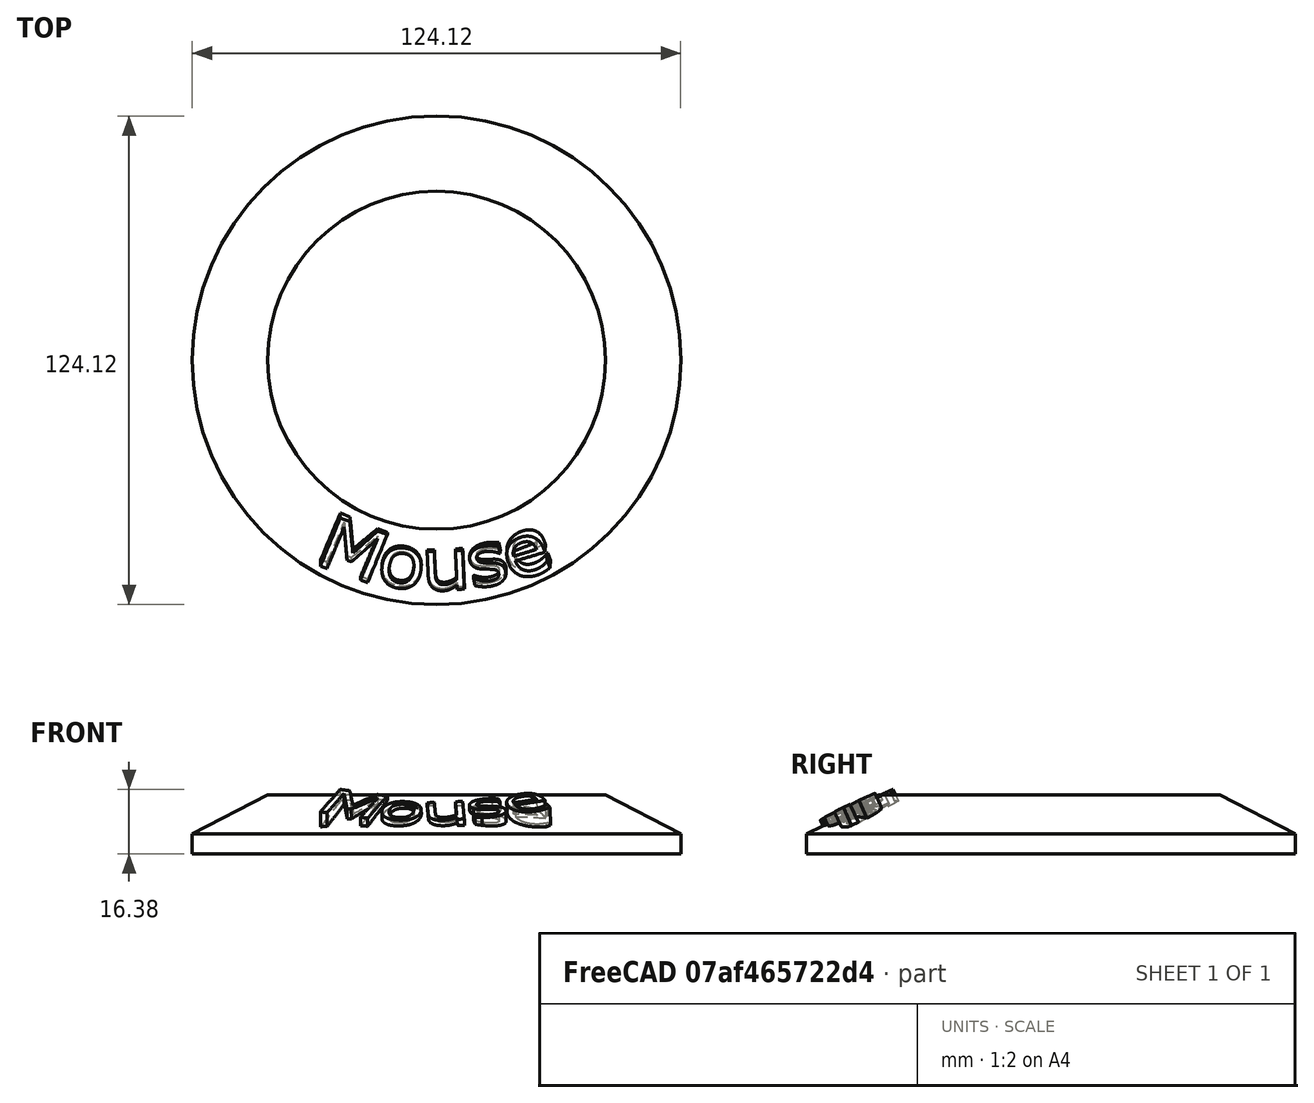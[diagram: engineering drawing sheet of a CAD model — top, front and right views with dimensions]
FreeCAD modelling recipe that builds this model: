
FCSTD DOCUMENT  (FreeCAD 0.19R24291 (Git))
Label: individual-ferret-with-base
License: All rights reserved
LicenseURL: http://en.wikipedia.org/wiki/All_rights_reserved
objects: Part::Feature×7, Part::Extrusion×7, Part::Cut×2, Part::MultiFuse×2, Mesh::Feature×1, Sketcher::SketchObject×1, PartDesign::Revolution×1, PartDesign::Body×1
note: 22 computed .brp shape members not serialized (recipe doc carries the construction recipe); baked Part::Feature solids carry a one-line shape summary decoded from their .brp

FEATURE [Part::Feature] Face
  shape: bbox 15.91 x 14.55 x 2e-07 mm, 1 faces, 0 solids (baked)
FEATURE [Part::Feature] Face001
  shape: bbox 11.7 x 10.66 x 2e-07 mm, 1 faces, 0 solids (baked)
FEATURE [Part::Feature] Face002
  shape: bbox 8.382 x 6.942 x 2e-07 mm, 1 faces, 0 solids (baked)
FEATURE [Part::Feature] Face003
  shape: bbox 12.99 x 13.22 x 2e-07 mm, 1 faces, 0 solids (baked)
FEATURE [Part::Feature] Face004
  shape: bbox 12.48 x 10.91 x 2e-07 mm, 1 faces, 0 solids (baked)
FEATURE [Part::Feature] Face005
  shape: bbox 11.17 x 12.16 x 2e-07 mm, 1 faces, 0 solids (baked)
FEATURE [Part::Feature] Face006
  shape: bbox 5.504 x 5.148 x 2e-07 mm, 1 faces, 0 solids (baked)
FEATURE [Part::Extrusion] Extrude
  Base = -> Face
  Dir = (0,0,-1)
  DirMode = 0
  FaceMakerClass = Part::FaceMakerBullseye
  LengthFwd = 5
  LengthRev = 0
  Solid = true
  Symmetric = false
FEATURE [Part::Extrusion] Extrude001
  Base = -> Face001
  Dir = (0,0,-1)
  DirMode = 0
  FaceMakerClass = Part::FaceMakerBullseye
  LengthFwd = 5
  LengthRev = 0
  Solid = true
  Symmetric = false
FEATURE [Part::Extrusion] Extrude002
  Base = -> Face002
  Dir = (0,0,-1)
  DirMode = 0
  FaceMakerClass = Part::FaceMakerBullseye
  LengthFwd = 5
  LengthRev = 0
  Solid = true
  Symmetric = false
FEATURE [Part::Extrusion] Extrude003
  Base = -> Face003
  Dir = (0,0,-1)
  DirMode = 0
  FaceMakerClass = Part::FaceMakerBullseye
  LengthFwd = 5
  LengthRev = 0
  Solid = true
  Symmetric = false
FEATURE [Part::Extrusion] Extrude004
  Base = -> Face004
  Dir = (0,0,-1)
  DirMode = 0
  FaceMakerClass = Part::FaceMakerBullseye
  LengthFwd = 5
  LengthRev = 0
  Solid = true
  Symmetric = false
FEATURE [Part::Extrusion] Extrude005
  Base = -> Face005
  Dir = (0,0,-1)
  DirMode = 0
  FaceMakerClass = Part::FaceMakerBullseye
  LengthFwd = 5
  LengthRev = 0
  Solid = true
  Symmetric = false
FEATURE [Part::Extrusion] Extrude006
  Base = -> Face006
  Dir = (0,0,-1)
  DirMode = 0
  FaceMakerClass = Part::FaceMakerBullseye
  LengthFwd = 5
  LengthRev = 0
  Solid = true
  Symmetric = false
FEATURE [Part::Cut] Cut
  Base = -> Extrude001
  Tool = -> Extrude002
FEATURE [Part::Cut] Cut001
  Base = -> Extrude005
  Tool = -> Extrude006
FEATURE [Part::MultiFuse] Fusion
  Placement = pos=(-115.728,-90.9275,-23.7897) rot=(0.324154,-0.216524,0.920892;1.15255rad)
  Shapes = -> [Extrude,Extrude003,Extrude004,Cut,Cut001]
FEATURE [Mesh::Feature] Ferret002  label="Ferret"
  Placement = pos=(-124.357,-109.694,-3.28686) rot=(0,0,1;0rad)
FEATURE [Sketcher::SketchObject] Sketch
  FullyConstrained = false
  MapMode = 5
  Placement = pos=(0,0,0) rot=(1,0,0;1.5708rad)
  Support = -> [XZ_Plane001]
  sketch-geometry (5):
    g0: LineSegment StartX=0 StartY=0 StartZ=0 EndX=-42.9267 EndY=0 EndZ=0
    g1: LineSegment StartX=-42.9267 StartY=0 StartZ=0 EndX=-62.0627 EndY=-9.87524 EndZ=0
    g2: LineSegment StartX=-62.0627 StartY=-9.87524 StartZ=0 EndX=-62.0627 EndY=-14.9492 EndZ=0
    g3: LineSegment StartX=-62.0627 StartY=-14.9492 StartZ=0 EndX=0 EndY=-14.9492 EndZ=0
    g4: LineSegment StartX=0 StartY=-14.9492 StartZ=0 EndX=0 EndY=0 EndZ=0
  constraints (10):
    c: Coincident(g-1,g0)
    c: PointOnObject(g0,g-1)
    c: Coincident(g0,g1)
    c: Coincident(g1,g2)
    c: Vertical(g2)
    c: Coincident(g2,g3)
    c: PointOnObject(g3,g-2)
    c: Horizontal(g3)
    c: Coincident(g3,g4)
    c: Coincident(g4,g0)
FEATURE [PartDesign::Revolution] Revolution
  Angle = 360
  Axis = (0,-2e-16,1)
  Base = (0,0,0)
  Placement = pos=(0,0,0) rot=(1,0,0;1.5708rad)
  Profile = -> Sketch
  ReferenceAxis = -> Sketch [V_Axis]
FEATURE [PartDesign::Body] Body001
  Group = -> [Sketch,Revolution]
  Origin = -> Origin001
  Tip = -> Revolution
FEATURE [Part::MultiFuse] Fusion001
  Shapes = -> [Fusion,Revolution]
